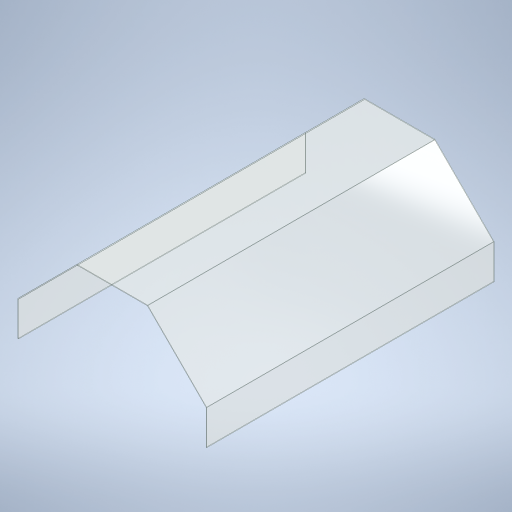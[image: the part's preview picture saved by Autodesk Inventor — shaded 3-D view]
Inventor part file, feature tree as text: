
AUTODESK INVENTOR PART (.ipt)
format: ipt  version: 2024 (Build 280153000, 153)  size: 269,312 bytes
history: native  units: in
note: dims shown in document units (in); Inventor stores cm internally (conversion verified against a paired STEP export)
features: extrude x1, sketch x1
ambient origin geometry x8: Origin, YZ Plane, XZ Plane, XY Plane, X Axis, Y Axis, Z Axis, Center Point
bodies: Solid1 (feature_tree)
feature tree (2):
  extrude  "Extrusion1"  TaperAngle=135.0deg  [1 undecoded]
  sketch  "Sketch1"  dims[d2=191.787in d3=135.0deg d4=71.787in d5=0.75in d6=291.5in d7=0.0in d8=35.25in d9=135.0deg d10=0.75in d11=0.75in d12=0.75in d13=135.0deg]
note: 1 required parameter value undecoded (feature->parameter linkage not recoverable at this tier; creation-order binding heuristic only, values carry confidence <= 0.55)
